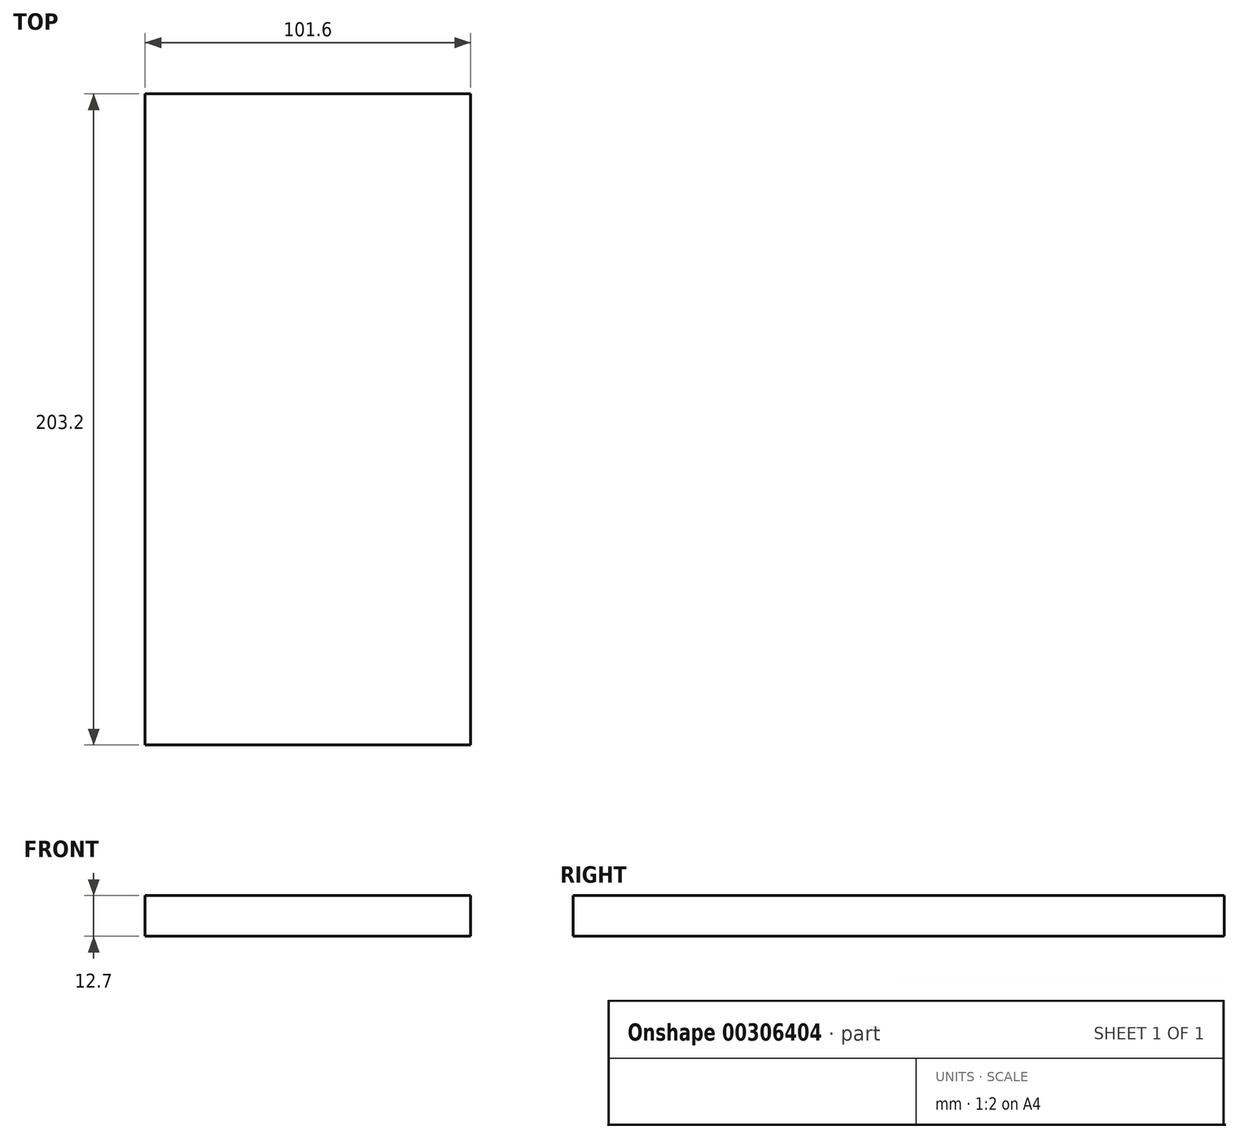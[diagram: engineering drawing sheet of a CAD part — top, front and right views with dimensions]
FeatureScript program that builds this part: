
annotation { "Feature Type Name" : "Feature", "Feature Type Description" : "" }
export const myFeature = defineFeature(function(context is Context, id is Id, definition is map)
    precondition{}
    {
        {
            var Q0;
            Q0=qCreatedBy(makeId("Top.planeOp"),FACE);
            var sketch = newSketch(context, id + "F0", { "sketchPlane" : qUnion([Q0])});
            skLineSegment(sketch, "E0.bottom", {"start": v(50.8, -101.6) * mm, "end": v(-50.8, -101.6) * mm});
            skLineSegment(sketch, "E0.top", {"start": v(50.8, 101.6) * mm, "end": v(-50.8, 101.6) * mm});
            skLineSegment(sketch, "E0.left", {"start": v(50.8, -101.6) * mm, "end": v(50.8, 101.6) * mm});
            skLineSegment(sketch, "E0.right", {"start": v(-50.8, -101.6) * mm, "end": v(-50.8, 101.6) * mm});
            skPoint(sketch, "E0.middle", {"position": v(0, 0) * mm});
            skSolve(sketch);
        }
        {
            var Q0;
            Q0 = qSketchRegion(id + "F0", true);
            extrude(context, id + "F1", {"entities" : qUnion([Q0]), "depth" : 12.7 * mm});
        }
    });
